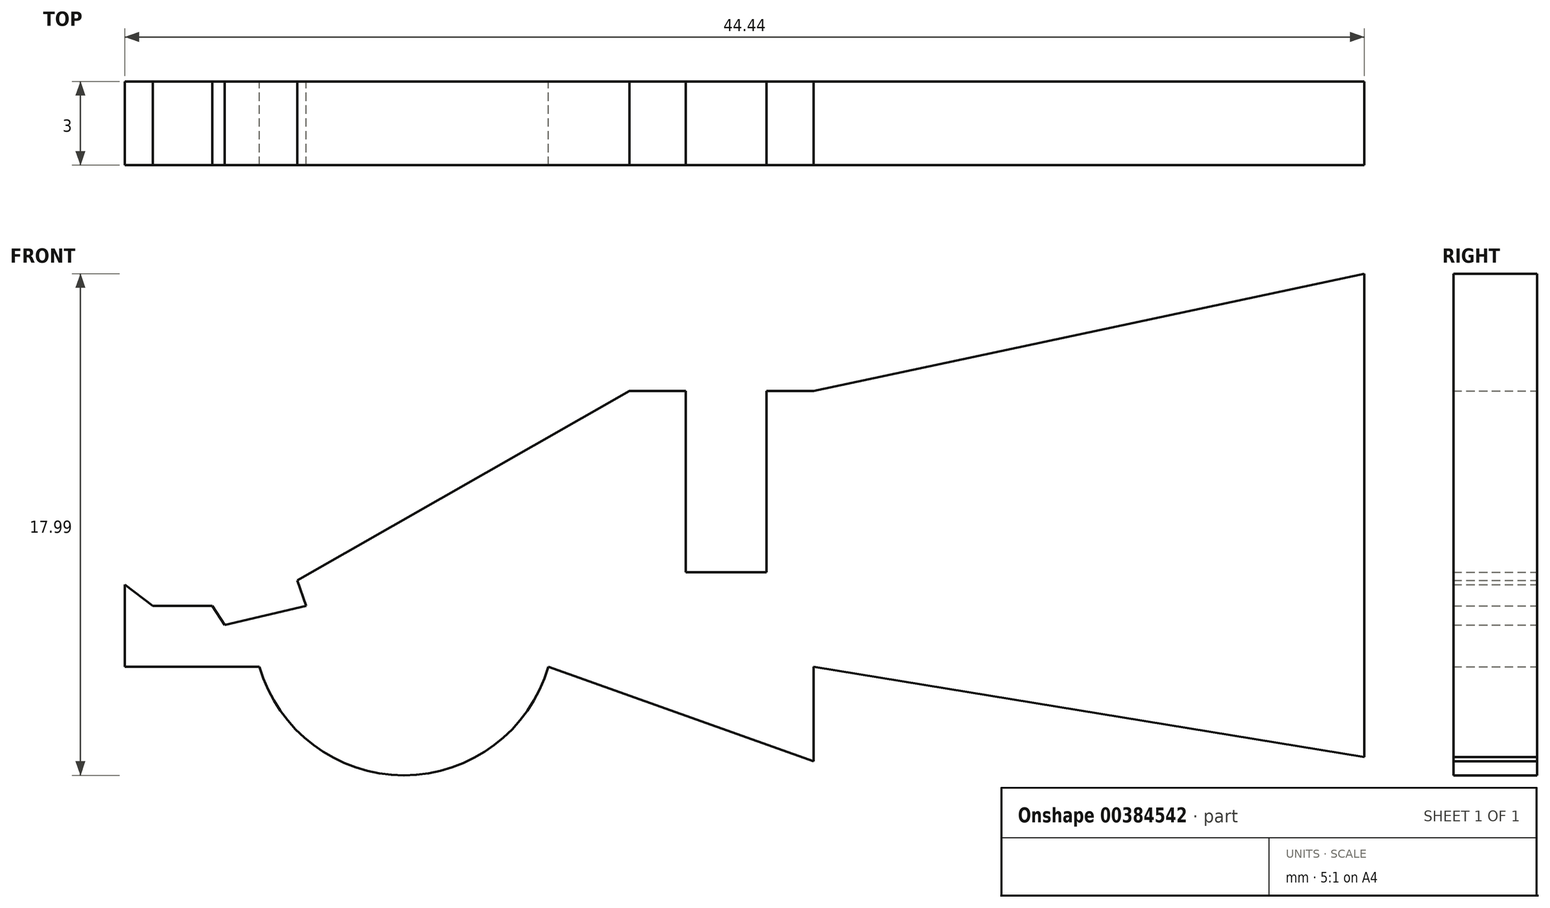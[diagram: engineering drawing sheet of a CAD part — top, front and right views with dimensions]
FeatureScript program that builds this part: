
annotation { "Feature Type Name" : "Feature", "Feature Type Description" : "" }
export const myFeature = defineFeature(function(context is Context, id is Id, definition is map)
    precondition{}
    {
        {
            var Q0;
            Q0=qCreatedBy(makeId("Front.planeOp"),FACE);
            var sketch = newSketch(context, id + "F0", { "sketchPlane" : qUnion([Q0])});
            skLineSegment(sketch, "E0", {"start": v(-24.7, 0) * mm, "end": v(-24.7, 2.94) * mm});
            skLineSegment(sketch, "E1", {"start": v(-24.7, 2.94) * mm, "end": v(-23.7, 2.18) * mm});
            skLineSegment(sketch, "E2", {"start": v(-23.7, 2.18) * mm, "end": v(-21.57, 2.18) * mm});
            skLineSegment(sketch, "E3", {"start": v(-24.7, 0) * mm, "end": v(-21.5, 0) * mm});
            skArc(sketch, "E4", {"start": v(-19.88, 0) * mm, "mid": v(-14.7, -3.9) * mm, "end": v(-9.52, 0) * mm});
            skLineSegment(sketch, "E5", {"start": v(-21.5, 0) * mm, "end": v(-19.88, 0) * mm});
            skLineSegment(sketch, "E6", {"start": v(-18.52, 3.1) * mm, "end": v(-6.6, 9.89) * mm});
            skLineSegment(sketch, "E7", {"start": v(-6.6, 9.89) * mm, "end": v(-4.6, 9.89) * mm});
            skLineSegment(sketch, "E8", {"start": v(0, 9.89) * mm, "end": v(19.74, 14.09) * mm});
            skLineSegment(sketch, "E9", {"start": v(19.74, 14.09) * mm, "end": v(19.74, -3.25) * mm});
            skLineSegment(sketch, "E10", {"start": v(19.74, -3.25) * mm, "end": v(0, 0) * mm});
            skLineSegment(sketch, "E11", {"start": v(0, 0) * mm, "end": v(0, -3.4) * mm});
            skLineSegment(sketch, "E12", {"start": v(0, -3.4) * mm, "end": v(-9.52, 0) * mm});
            skLineSegment(sketch, "E13", {"start": v(-21.57, 2.18) * mm, "end": v(-21.13, 1.5) * mm});
            skLineSegment(sketch, "E14", {"start": v(-21.13, 1.5) * mm, "end": v(-18.2, 2.18) * mm});
            skLineSegment(sketch, "E15", {"start": v(-18.2, 2.18) * mm, "end": v(-18.52, 3.1) * mm});
            skLineSegment(sketch, "E16.top", {"start": v(-4.6, 3.39) * mm, "end": v(-1.7, 3.39) * mm});
            skLineSegment(sketch, "E16.left", {"start": v(-4.6, 9.89) * mm, "end": v(-4.6, 3.39) * mm});
            skLineSegment(sketch, "E16.right", {"start": v(-1.7, 9.89) * mm, "end": v(-1.7, 3.39) * mm});
            skLineSegment(sketch, "E17.trimOffspring", {"start": v(-1.7, 9.89) * mm, "end": v(0, 9.89) * mm});
            skSolve(sketch);
        }
        {
            var Q0;
            Q0 = qSketchRegion(id + "F0", true);
            extrude(context, id + "F1", {"entities" : qUnion([Q0]), "depth" : 3 * mm});
        }
        {
            var Q0;
            Q0 = qSketchRegion(id + "F0", true);
            extrude(context, id + "F2", {"entities" : qUnion([Q0]), "operationType" : NewBodyOperationType.ADD, "depth" : 3 * mm});
        }
    });
